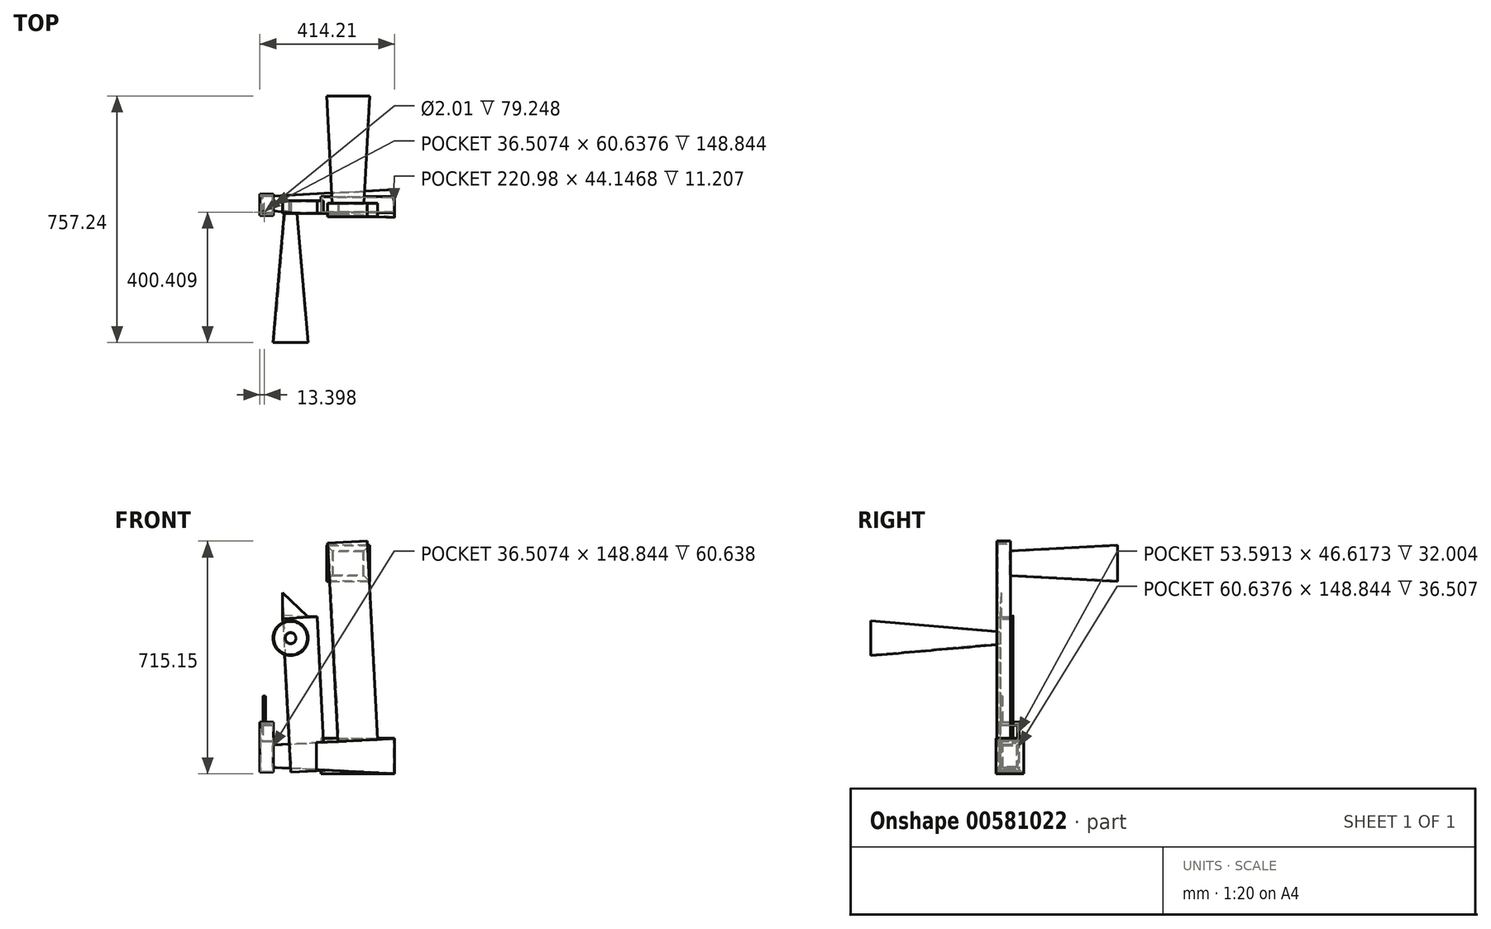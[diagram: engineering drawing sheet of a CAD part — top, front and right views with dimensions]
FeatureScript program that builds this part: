
annotation { "Feature Type Name" : "Feature", "Feature Type Description" : "" }
export const myFeature = defineFeature(function(context is Context, id is Id, definition is map)
    precondition{}
    {
        {
            var Q0;
            Q0=qCreatedBy(makeId("Top.planeOp"),FACE);
            var sketch = newSketch(context, id + "F0", { "sketchPlane" : qUnion([Q0])});
            skLineSegment(sketch, "E0.bottom", {"start": v(-41.59, 42.52) * mm, "end": v(0, 42.52) * mm});
            skLineSegment(sketch, "E0.top", {"start": v(-41.59, -23.2) * mm, "end": v(0, -23.2) * mm});
            skLineSegment(sketch, "E0.left", {"start": v(-41.59, 42.52) * mm, "end": v(-41.59, -23.2) * mm});
            skLineSegment(sketch, "E0.right", {"start": v(0, 42.52) * mm, "end": v(0, -23.2) * mm});
            skSolve(sketch);
        }
        {
            var Q0;
            Q0=makeQuery(id+"F0.imprint","IMPRINT",FACE,{"disambiguationData":[TD([[makeQuery(id+"F0.imprint","IMPRINT",EDGE,{"derivedFrom":sQuery(id+"F0.wireOp",EDGE,"E0.bottom")}),-1.0]])]});
            extrude(context, id + "F1", {"entities" : qUnion([Q0]), "depth" : 153.92 * mm, "offsetDistance" : 25.4 * mm});
        }
        {
            var Q0;
            Q0=makeQuery(id+"F1.opExtrude","CAP_FACE",FACE,{"disambiguationData":[OSD([sQuery(id+"F0.wireOp",EDGE,"E0.bottom"),sQuery(id+"F0.wireOp",EDGE,"E0.top"),sQuery(id+"F0.wireOp",EDGE,"E0.left"),sQuery(id+"F0.wireOp",EDGE,"E0.right")])],"isStart":false});
            var sketch = newSketch(context, id + "F2", { "sketchPlane" : qUnion([Q0])});
            skCircle(sketch, "E1", {"center": v(-28.2, -12.96) * mm, "radius": 3.54 * mm});
            skSolve(sketch);
        }
        {
            var Q0;
            Q0 = qSketchRegion(id + "F2", true);
            extrude(context, id + "F3", {"entities" : qUnion([Q0]), "operationType" : NewBodyOperationType.ADD, "depth" : 79.25 * mm, "offsetDistance" : 25.4 * mm});
        }
        {
            var Q0;
            Q0=makeQuery(id+"F1.opExtrude","SWEPT_FACE",FACE,{"disambiguationData":[OSD([sQuery(id+"F0.wireOp",EDGE,"E0.right")])]});
            var sketch = newSketch(context, id + "F4", { "sketchPlane" : qUnion([Q0])});
            skLineSegment(sketch, "E2.bottom", {"start": v(-16.95, 143.1) * mm, "end": v(36.64, 143.1) * mm});
            skLineSegment(sketch, "E2.top", {"start": v(-16.95, 96.48) * mm, "end": v(36.64, 96.48) * mm});
            skLineSegment(sketch, "E2.left", {"start": v(-16.95, 143.1) * mm, "end": v(-16.95, 96.48) * mm});
            skLineSegment(sketch, "E2.right", {"start": v(36.64, 143.1) * mm, "end": v(36.64, 96.48) * mm});
            skSolve(sketch);
        }
        {
            var Q0;
            Q0=makeQuery(id+"F4.imprint","IMPRINT",FACE,{"disambiguationData":[TD([[makeQuery(id+"F4.imprint","IMPRINT",EDGE,{"derivedFrom":sQuery(id+"F4.wireOp",EDGE,"E2.bottom")}),-1.0]])]});
            extrude(context, id + "F5", {"entities" : qUnion([Q0]), "operationType" : NewBodyOperationType.REMOVE, "oppositeDirection" : true, "depth" : 32 * mm, "offsetDistance" : 25.4 * mm});
        }
        {
            var Q0;
            Q0=makeQuery(id+"F1.opExtrude","SWEPT_FACE",FACE,{"disambiguationData":[OSD([sQuery(id+"F0.wireOp",EDGE,"E0.right")])]});
            var sketch = newSketch(context, id + "F6", { "sketchPlane" : qUnion([Q0])});
            skLineSegment(sketch, "E3.bottom", {"start": v(-10.2, 84.01) * mm, "end": v(36.35, 84.01) * mm});
            skLineSegment(sketch, "E3.top", {"start": v(-10.2, 13.93) * mm, "end": v(36.35, 13.93) * mm});
            skLineSegment(sketch, "E3.left", {"start": v(-10.2, 84.01) * mm, "end": v(-10.2, 13.93) * mm});
            skLineSegment(sketch, "E3.right", {"start": v(36.35, 84.01) * mm, "end": v(36.35, 13.93) * mm});
            skSolve(sketch);
        }
        {
            var Q0;
            Q0=makeQuery(id+"F6.imprint","IMPRINT",FACE,{"disambiguationData":[TD([[makeQuery(id+"F6.imprint","IMPRINT",EDGE,{"derivedFrom":sQuery(id+"F6.wireOp",EDGE,"E3.bottom")}),-1.0]])]});
            extrude(context, id + "F7", {"entities" : qUnion([Q0]), "operationType" : NewBodyOperationType.ADD, "depth" : 372.62 * mm, "offsetDistance" : 25.4 * mm, "hasDraft" : true, "draftAngle" : 3 * degree});
        }
        {
            var Q0;
            Q0=makeQuery(id+"F7.opExtrude","SWEPT_FACE",FACE,{"disambiguationData":[OSD([sQuery(id+"F6.wireOp",EDGE,"E3.bottom")])]});
            var sketch = newSketch(context, id + "F8", { "sketchPlane" : qUnion([Q0])});
            skLineSegment(sketch, "E4.bottom", {"start": v(57.43, 18.13) * mm, "end": v(329.57, 18.13) * mm});
            skLineSegment(sketch, "E4.top", {"start": v(57.43, -12.59) * mm, "end": v(329.57, -12.59) * mm});
            skLineSegment(sketch, "E4.left", {"start": v(57.43, 18.13) * mm, "end": v(57.43, -12.59) * mm});
            skLineSegment(sketch, "E4.right", {"start": v(329.57, 18.13) * mm, "end": v(329.57, -12.59) * mm});
            skSolve(sketch);
        }
        {
            var Q0;
            Q0=makeQuery(id+"F8.imprint","IMPRINT",FACE,{"disambiguationData":[TD([[makeQuery(id+"F8.imprint","IMPRINT",EDGE,{"derivedFrom":sQuery(id+"F8.wireOp",EDGE,"E4.bottom")}),-1.0]])]});
            extrude(context, id + "F9", {"entities" : qUnion([Q0]), "operationType" : NewBodyOperationType.ADD, "oppositeDirection" : true, "depth" : 86.61 * mm, "offsetDistance" : 25.4 * mm, "hasDraft" : true, "draftAngle" : 3 * degree});
        }
        {
            var Q0;
            Q0=makeQuery(id+"F9.opExtrude","CAP_FACE",FACE,{"disambiguationData":[OSD([sQuery(id+"F8.wireOp",EDGE,"E4.bottom"),sQuery(id+"F8.wireOp",EDGE,"E4.top"),sQuery(id+"F8.wireOp",EDGE,"E4.left"),sQuery(id+"F8.wireOp",EDGE,"E4.right")])],"isStart":false});
            var Q1;
            Q1=makeQuery(id+"F9.opExtrude","SWEPT_FACE",FACE,{"disambiguationData":[OSD([sQuery(id+"F8.wireOp",EDGE,"E4.top")])]});
            var Q2;
            Q2=makeQuery(id+"F9.opExtrude","SWEPT_FACE",FACE,{"disambiguationData":[OSD([sQuery(id+"F8.wireOp",EDGE,"E4.bottom")])]});
            extrude(context, id + "F10", {"entities" : qUnion([Q0, Q1, Q2]), "operationType" : NewBodyOperationType.ADD, "oppositeDirection" : true, "depth" : 471.93 * mm, "offsetDistance" : 25.4 * mm});
        }
        {
            var Q0;
            Q0=makeQuery(id+"F7.opExtrude","SWEPT_FACE",FACE,{"disambiguationData":[OSD([sQuery(id+"F6.wireOp",EDGE,"E3.bottom")])]});
            var sketch = newSketch(context, id + "F11", { "sketchPlane" : qUnion([Q0])});
            skLineSegment(sketch, "E5.bottom", {"start": v(324.84, -26.97) * mm, "end": v(203.32, -26.97) * mm});
            skLineSegment(sketch, "E5.top", {"start": v(324.84, 15) * mm, "end": v(203.32, 15) * mm});
            skLineSegment(sketch, "E5.left", {"start": v(324.84, -26.97) * mm, "end": v(324.84, 15) * mm});
            skLineSegment(sketch, "E5.right", {"start": v(203.32, -26.97) * mm, "end": v(203.32, 15) * mm});
            skSolve(sketch);
        }
        {
            var Q0;
            Q0 = qSketchRegion(id + "F11", true);
            extrude(context, id + "F12", {"entities" : qUnion([Q0]), "operationType" : NewBodyOperationType.ADD, "depth" : 609.6 * mm, "offsetDistance" : 25.4 * mm});
        }
        {
            var Q0;
            Q0=makeQuery(id+"F7.opExtrude","CAP_FACE",FACE,{"disambiguationData":[OSD([sQuery(id+"F6.wireOp",EDGE,"E3.bottom"),sQuery(id+"F6.wireOp",EDGE,"E3.top"),sQuery(id+"F6.wireOp",EDGE,"E3.left"),sQuery(id+"F6.wireOp",EDGE,"E3.right")])],"isStart":false});
            var sketch = newSketch(context, id + "F13", { "sketchPlane" : qUnion([Q0])});
            skLineSegment(sketch, "E6.bottom", {"start": v(-14.2, 103.54) * mm, "end": v(35.03, 103.54) * mm});
            skLineSegment(sketch, "E6.top", {"start": v(-14.2, -5.6) * mm, "end": v(35.03, -5.6) * mm});
            skLineSegment(sketch, "E6.left", {"start": v(-14.2, 103.54) * mm, "end": v(-14.2, -5.6) * mm});
            skLineSegment(sketch, "E6.right", {"start": v(35.03, 103.54) * mm, "end": v(35.03, -5.6) * mm});
            skSolve(sketch);
        }
        {
            var Q0;
            Q0 = qSketchRegion(id + "F13", true);
            extrude(context, id + "F14", {"entities" : qUnion([Q0]), "operationType" : NewBodyOperationType.ADD, "oppositeDirection" : true, "depth" : 226.06 * mm, "offsetDistance" : 25.4 * mm});
        }
        {
            var Q0;
            Q0=makeQuery(id+"F12.opExtrude","SWEPT_FACE",FACE,{"disambiguationData":[OSD([sQuery(id+"F11.wireOp",EDGE,"E5.bottom")])]});
            var sketch = newSketch(context, id + "F15", { "sketchPlane" : qUnion([Q0])});
            skLineSegment(sketch, "E7.bottom", {"start": v(182.93, 677.77) * mm, "end": v(276.16, 677.77) * mm});
            skLineSegment(sketch, "E7.top", {"start": v(182.93, 605.28) * mm, "end": v(276.16, 605.28) * mm});
            skLineSegment(sketch, "E7.left", {"start": v(182.93, 677.77) * mm, "end": v(182.93, 605.28) * mm});
            skLineSegment(sketch, "E7.right", {"start": v(276.16, 677.77) * mm, "end": v(276.16, 605.28) * mm});
            skSolve(sketch);
        }
        {
            var Q0;
            Q0 = qSketchRegion(id + "F15", true);
            extrude(context, id + "F16", {"entities" : qUnion([Q0]), "operationType" : NewBodyOperationType.ADD, "oppositeDirection" : true, "depth" : 370.84 * mm, "offsetDistance" : 25.4 * mm, "hasDraft" : true, "draftAngle" : 3 * degree});
        }
        {
            var Q0;
            Q0=makeQuery(id+"F10.opExtrude","SWEPT_FACE",FACE,{"disambiguationData":[OSD([sQuery(id+"F8.wireOp",EDGE,"E4.top")]),OD(0.0)]});
            var sketch = newSketch(context, id + "F17", { "sketchPlane" : qUnion([Q0])});
            skCircle(sketch, "E8", {"center": v(52.85, 411.52) * mm, "radius": 19.21 * mm});
            skSolve(sketch);
        }
        {
            var Q0;
            Q0=makeQuery(id+"F17.imprint","IMPRINT",FACE,{"disambiguationData":[TD([[makeQuery(id+"F17.imprint","IMPRINT",EDGE,{"derivedFrom":sQuery(id+"F17.wireOp",EDGE,"E8")}),1.0]])]});
            extrude(context, id + "F18", {"entities" : qUnion([Q0]), "operationType" : NewBodyOperationType.ADD, "depth" : 396.24 * mm, "offsetDistance" : 25.4 * mm, "hasDraft" : true, "draftAngle" : 5 * degree});
        }
        {
            var Q0;
            Q0=makeQuery(id+"F18.opExtrude","CAP_FACE",FACE,{"disambiguationData":[OSD([sQuery(id+"F17.wireOp",EDGE,"E8")])],"isStart":false});
            shell(context, id + "F19", {"entities" : qUnion([Q0]), "thickness" : 2.54 * mm});
        }
    });
